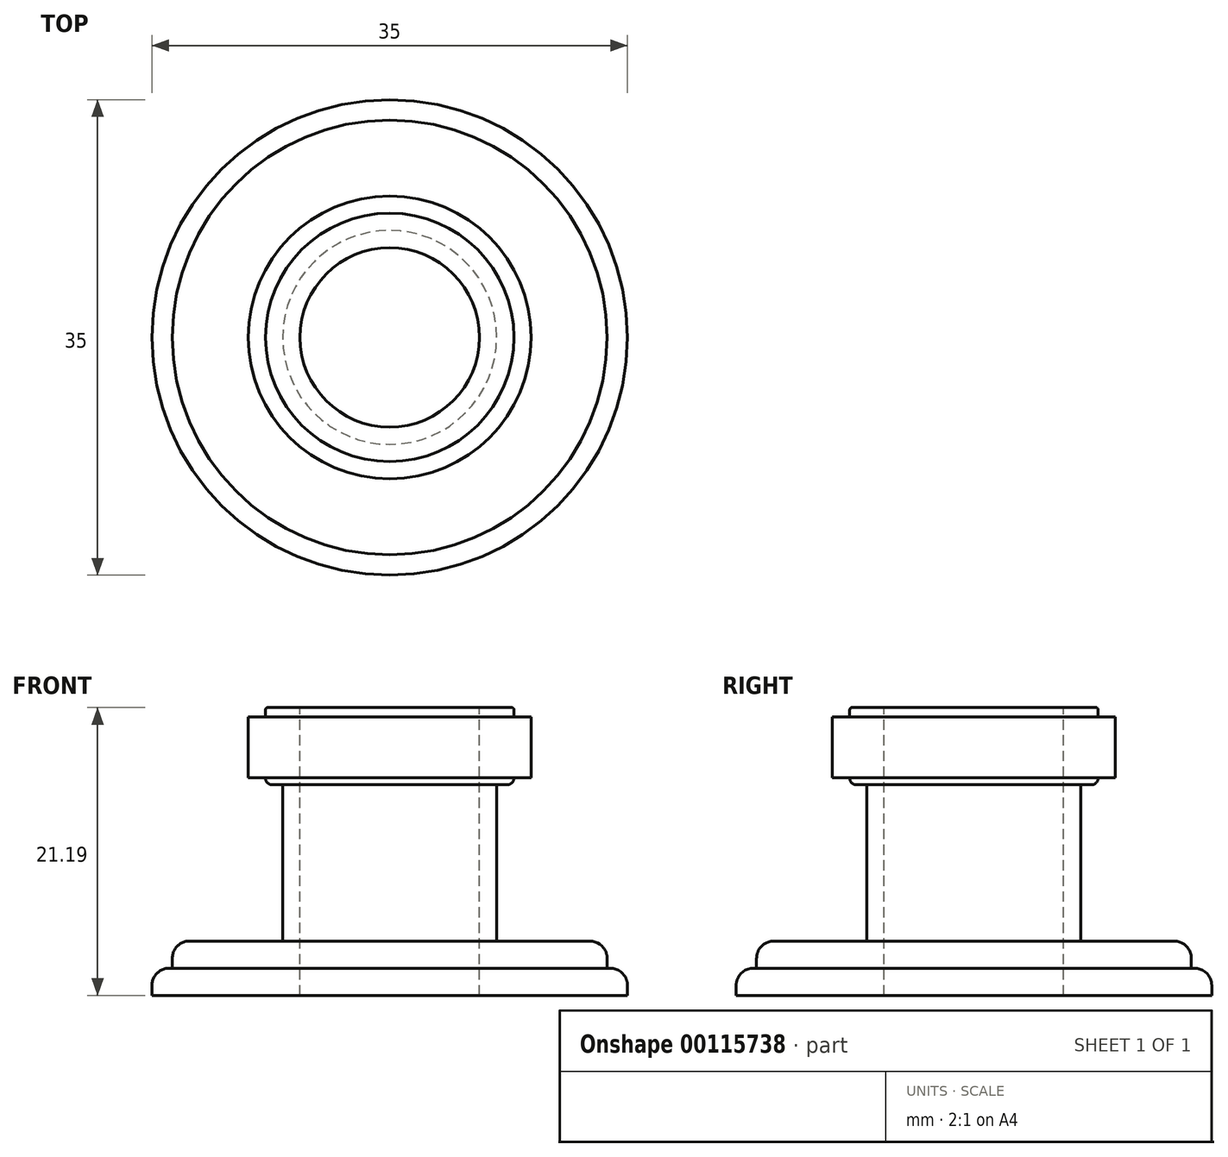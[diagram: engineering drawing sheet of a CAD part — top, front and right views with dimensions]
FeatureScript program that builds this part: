
annotation { "Feature Type Name" : "Feature", "Feature Type Description" : "" }
export const myFeature = defineFeature(function(context is Context, id is Id, definition is map)
    precondition{}
    {
        {
            var Q0;
            Q0=qCreatedBy(makeId("Front.planeOp"),FACE);
            var sketch = newSketch(context, id + "F0", { "sketchPlane" : qUnion([Q0])});
            skLineSegment(sketch, "E0", {"start": v(0, 0) * mm, "end": v(-17.5, 0) * mm});
            skLineSegment(sketch, "E1", {"start": v(-17.5, 0) * mm, "end": v(-17.5, 2) * mm});
            skLineSegment(sketch, "E2", {"start": v(-17.5, 2) * mm, "end": v(-16, 2) * mm});
            skLineSegment(sketch, "E3", {"start": v(-16, 2) * mm, "end": v(-16, 4) * mm});
            skLineSegment(sketch, "E4", {"start": v(-16, 4) * mm, "end": v(-7.87, 4) * mm});
            skLineSegment(sketch, "E5", {"start": v(-7.87, 4) * mm, "end": v(-7.87, 15.5) * mm});
            skLineSegment(sketch, "E6", {"start": v(-7.87, 15.5) * mm, "end": v(-9.14, 15.5) * mm});
            skLineSegment(sketch, "E7", {"start": v(-9.14, 15.5) * mm, "end": v(-9.14, 16) * mm});
            skLineSegment(sketch, "E8", {"start": v(-9.14, 16) * mm, "end": v(-10.41, 16) * mm});
            skLineSegment(sketch, "E9", {"start": v(-10.41, 16) * mm, "end": v(-10.41, 20.5) * mm});
            skLineSegment(sketch, "E10", {"start": v(-10.41, 20.5) * mm, "end": v(-9.14, 20.5) * mm});
            skLineSegment(sketch, "E11", {"start": v(-9.14, 20.5) * mm, "end": v(-9.14, 21.02) * mm});
            skLineSegment(sketch, "E12", {"start": v(-8.97, 21.2) * mm, "end": v(0, 21.2) * mm});
            skLineSegment(sketch, "E13", {"start": v(0, 21.2) * mm, "end": v(0, 0) * mm});
            skLineSegment(sketch, "E14", {"start": v(-6.6, 21.2) * mm, "end": v(-6.6, 0) * mm});
            skPoint(sketch, "E15.visualSharp", {"position": v(-9.14, 21.2) * mm});
            skArc(sketch, "E15.filletArc", {"start": v(-8.97, 21.2) * mm, "mid": v(-9.1, 21.14) * mm, "end": v(-9.14, 21.02) * mm});
            skSolve(sketch);
        }
        {
            var Q0;
            {var subQ0=sQuery(id+"F0.wireOp",EDGE,"E1");Q0=makeQuery(id+"F0.imprint","IMPRINT",FACE,{"disambiguationData":[TD([[makeQuery(id+"F0.imprint","IMPRINT",EDGE,{"derivedFrom":subQ0}),-1.0]])]});}
            var Q1;
            Q1=sQuery(id+"F0.wireOp",EDGE,"E13");
            revolve(context, id + "F1", {"entities" : qUnion([Q0]), "axis" : qUnion([Q1]), "revolveType" : RevolveType.FULL});
        }
        {
            var Q0;
            Q0=makeQuery(id+"F1.opRevolve","SWEPT_EDGE",EDGE,{"disambiguationData":[OSD([sQuery(id+"F0.wireOp",EDGE,"E3"),sQuery(id+"F0.wireOp",EDGE,"E4")])]});
            var Q1;
            Q1=makeQuery(id+"F1.opRevolve","SWEPT_EDGE",EDGE,{"disambiguationData":[OSD([sQuery(id+"F0.wireOp",EDGE,"E1"),sQuery(id+"F0.wireOp",EDGE,"E2")])]});
            fillet(context, id + "F2", {"entities" : qUnion([Q0, Q1]), "radius" : 1.27 * mm, "tangentPropagation" : true, "allowEdgeOverflow" : false});
        }
        {
            var Q0;
            Q0=makeQuery(id+"F1.opRevolve","SWEPT_EDGE",EDGE,{"disambiguationData":[OSD([sQuery(id+"F0.wireOp",EDGE,"E6"),sQuery(id+"F0.wireOp",EDGE,"E7")])]});
            fillet(context, id + "F3", {"entities" : qUnion([Q0]), "radius" : 0.5 * mm, "tangentPropagation" : true, "allowEdgeOverflow" : false});
        }
    });
